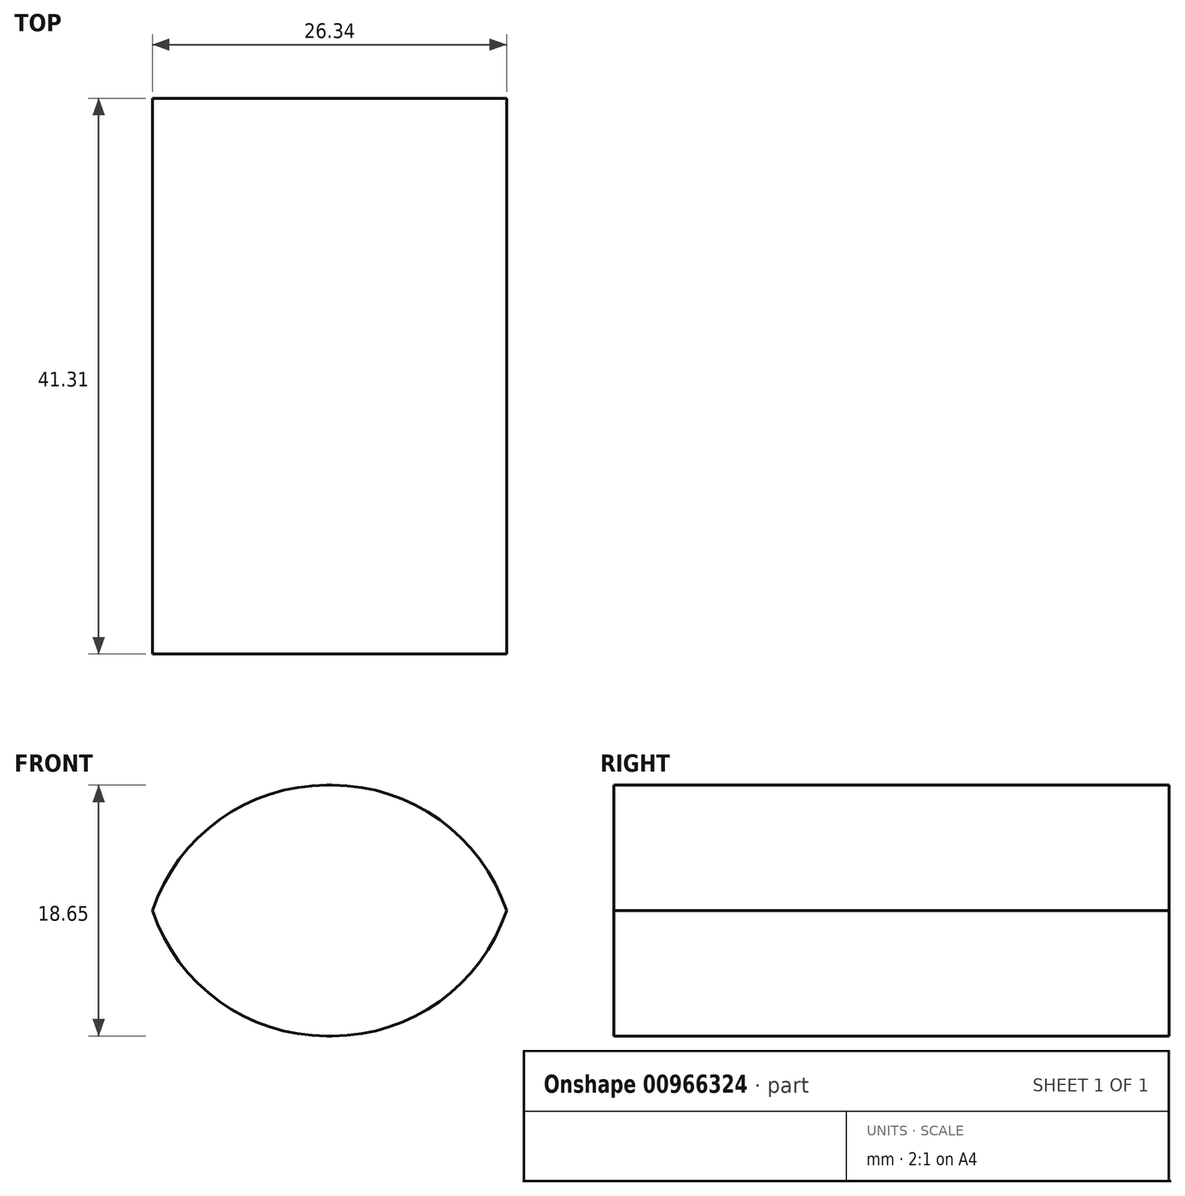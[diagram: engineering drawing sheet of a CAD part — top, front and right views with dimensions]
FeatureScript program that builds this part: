
annotation { "Feature Type Name" : "Feature", "Feature Type Description" : "" }
export const myFeature = defineFeature(function(context is Context, id is Id, definition is map)
    precondition{}
    {
        {
            var Q0;
            Q0=qCreatedBy(makeId("Top.planeOp"),FACE);
            var sketch = newSketch(context, id + "F0", { "sketchPlane" : qUnion([Q0])});
            skLineSegment(sketch, "E0.bottom", {"start": v(0, 0) * mm, "end": v(45.03, 0) * mm});
            skLineSegment(sketch, "E0.top", {"start": v(0, 0) * mm, "end": v(45.03, 0) * mm});
            skLineSegment(sketch, "E0.left", {"start": v(0, 0) * mm, "end": v(0, 0) * mm});
            skLineSegment(sketch, "E0.right", {"start": v(45.03, 0) * mm, "end": v(45.03, 0) * mm});
            skLineSegment(sketch, "E1.bottom", {"start": v(41.63, -28.61) * mm, "end": v(13.87, -28.61) * mm});
            skLineSegment(sketch, "E1.top", {"start": v(41.63, -69.92) * mm, "end": v(13.87, -69.92) * mm});
            skLineSegment(sketch, "E1.left", {"start": v(41.63, -28.61) * mm, "end": v(41.63, -69.92) * mm});
            skLineSegment(sketch, "E1.right", {"start": v(13.87, -28.61) * mm, "end": v(13.87, -69.92) * mm});
            skSolve(sketch);
        }
        {
            var Q0;
            Q0 = qSketchRegion(id + "F0", true);
            var Q1;
            Q1=makeQuery(id+"F0.imprint","IMPRINT",FACE,{"disambiguationData":[TD([[makeQuery(id+"F0.imprint","IMPRINT",EDGE,{"derivedFrom":sQuery(id+"F0.wireOp",EDGE,"E1.bottom")}),1.0]])]});
            extrude(context, id + "F1", {"entities" : qUnion([Q0, Q1]), "depth" : 18.65 * mm, "offsetDistance" : 25.4 * mm});
        }
        {
            var Q0;
            Q0=makeQuery(id+"F1.opExtrude","CAP_EDGE",EDGE,{"disambiguationData":[OSD([sQuery(id+"F0.wireOp",EDGE,"E1.left")])],"isStart":false});
            var Q1;
            Q1=makeQuery(id+"F1.opExtrude","CAP_EDGE",EDGE,{"disambiguationData":[OSD([sQuery(id+"F0.wireOp",EDGE,"E1.right")])],"isStart":false});
            var Q2;
            Q2=makeQuery(id+"F1.opExtrude","CAP_EDGE",EDGE,{"disambiguationData":[OSD([sQuery(id+"F0.wireOp",EDGE,"E1.left")])],"isStart":true});
            var Q3;
            Q3=makeQuery(id+"F1.opExtrude","CAP_EDGE",EDGE,{"disambiguationData":[OSD([sQuery(id+"F0.wireOp",EDGE,"E1.right")])],"isStart":true});
            fillet(context, id + "F2", {"entities" : qUnion([Q0, Q1, Q2, Q3]), "radius" : 13.66 * mm, "tangentPropagation" : true, "allowEdgeOverflow" : false});
        }
    });
